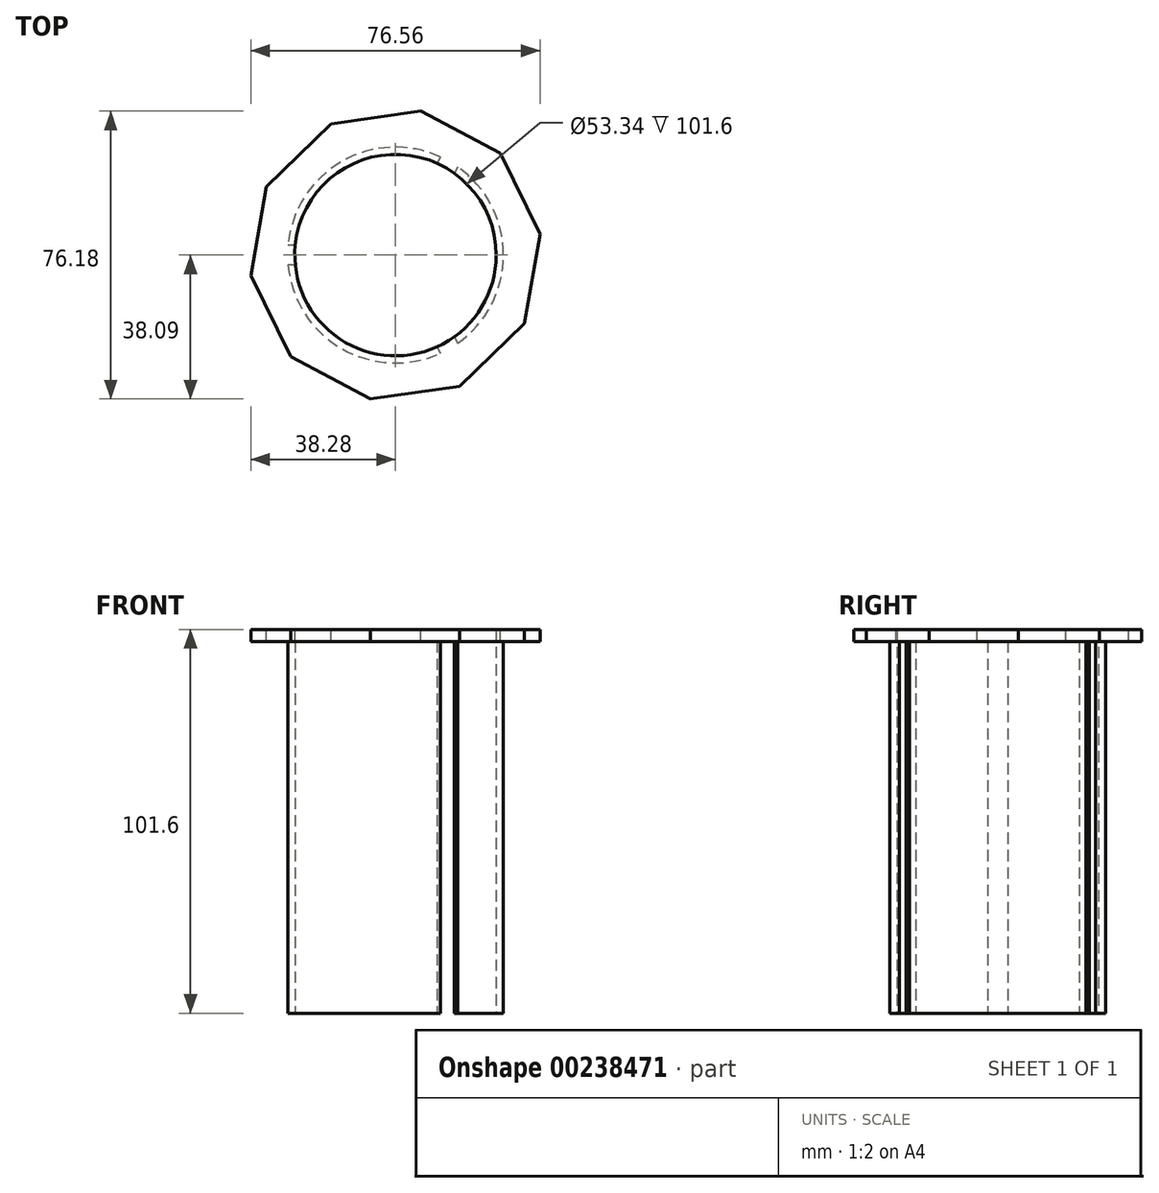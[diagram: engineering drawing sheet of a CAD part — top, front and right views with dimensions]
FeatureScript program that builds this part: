
annotation { "Feature Type Name" : "Feature", "Feature Type Description" : "" }
export const myFeature = defineFeature(function(context is Context, id is Id, definition is map)
    precondition{}
    {
        {
            var Q0;
            Q0=qCreatedBy(makeId("Top.planeOp"),FACE);
            var sketch = newSketch(context, id + "F0", { "sketchPlane" : qUnion([Q0])});
            skCircle(sketch, "E0", {"center": v(0, 0) * mm, "radius": 28.58 * mm});
            skCircle(sketch, "E1", {"center": v(0, 0) * mm, "radius": 26.67 * mm});
            skSolve(sketch);
        }
        {
            var Q0;
            Q0=makeQuery(id+"F0.imprint","IMPRINT",FACE,{"disambiguationData":[TD([[makeQuery(id+"F0.imprint","IMPRINT",EDGE,{"derivedFrom":sQuery(id+"F0.wireOp",EDGE,"E0")}),1.0]])]});
            extrude(context, id + "F1", {"entities" : qUnion([Q0]), "depth" : 101.6 * mm});
        }
        {
            var Q0;
            Q0=makeQuery(id+"F1.opExtrude","CAP_FACE",FACE,{"disambiguationData":[OSD([sQuery(id+"F0.wireOp",EDGE,"E0"),sQuery(id+"F0.wireOp",EDGE,"E1")])],"isStart":false});
            var sketch = newSketch(context, id + "F2", { "sketchPlane" : qUnion([Q0])});
            skCircle(sketch, "E2.cCircle", {"center": v(0, 0) * mm, "radius": 38.67 * mm, "construction": true});
            skLineSegment(sketch, "E2.0", {"start": v(-34.18, 18.1) * mm, "end": v(-17.01, 34.72) * mm});
            skLineSegment(sketch, "E2.1", {"start": v(-17.01, 34.72) * mm, "end": v(6.65, 38.1) * mm});
            skLineSegment(sketch, "E2.2", {"start": v(6.65, 38.1) * mm, "end": v(27.77, 26.91) * mm});
            skLineSegment(sketch, "E2.3", {"start": v(27.77, 26.91) * mm, "end": v(38.28, 5.45) * mm});
            skLineSegment(sketch, "E2.4", {"start": v(38.28, 5.45) * mm, "end": v(34.18, -18.1) * mm});
            skLineSegment(sketch, "E2.5", {"start": v(34.18, -18.1) * mm, "end": v(17.01, -34.72) * mm});
            skLineSegment(sketch, "E2.6", {"start": v(17.01, -34.72) * mm, "end": v(-6.65, -38.1) * mm});
            skLineSegment(sketch, "E2.7", {"start": v(-6.65, -38.1) * mm, "end": v(-27.77, -26.91) * mm});
            skLineSegment(sketch, "E2.8", {"start": v(-27.77, -26.91) * mm, "end": v(-38.28, -5.45) * mm});
            skLineSegment(sketch, "E2.9", {"start": v(-38.28, -5.45) * mm, "end": v(-34.18, 18.1) * mm});
            skCircle(sketch, "E3", {"center": v(0, 0) * mm, "radius": 28.2 * mm});
            skSolve(sketch);
        }
        {
            var Q0;
            Q0=makeQuery(id+"F2.imprint","IMPRINT",FACE,{"disambiguationData":[TD([[makeQuery(id+"F2.imprint","IMPRINT",EDGE,{"derivedFrom":sQuery(id+"F2.wireOp",EDGE,"E2.0")}),-1.0]])]});
            extrude(context, id + "F3", {"entities" : qUnion([Q0]), "operationType" : NewBodyOperationType.ADD, "oppositeDirection" : true, "depth" : 3.17 * mm});
        }
        {
            var Q0;
            Q0=makeQuery(id+"F1.opExtrude","CAP_FACE",FACE,{"disambiguationData":[OSD([sQuery(id+"F0.wireOp",EDGE,"E0"),sQuery(id+"F0.wireOp",EDGE,"E1")])],"isStart":true});
            var sketch = newSketch(context, id + "F4", { "sketchPlane" : qUnion([Q0])});
            skCircle(sketch, "E4.cCircle", {"center": v(0, 0) * mm, "radius": 1.52 * mm, "construction": true});
            skLineSegment(sketch, "E4.0", {"start": v(3.04, 0) * mm, "end": v(-1.52, -2.63) * mm});
            skLineSegment(sketch, "E4.1", {"start": v(-1.52, -2.63) * mm, "end": v(-1.52, 2.63) * mm});
            skLineSegment(sketch, "E4.2", {"start": v(-1.52, 2.63) * mm, "end": v(3.04, 0) * mm});
            skPoint(sketch, "E4.0.midPoint", {"position": v(0.76, -1.31) * mm});
            skLineSegment(sketch, "E5.bottom", {"start": v(-1.52, -2.63) * mm, "end": v(-52.32, -2.63) * mm});
            skLineSegment(sketch, "E5.top", {"start": v(-1.52, 2.63) * mm, "end": v(-52.32, 2.63) * mm});
            skLineSegment(sketch, "E5.right", {"start": v(-52.32, -2.63) * mm, "end": v(-52.32, 2.63) * mm});
            skLineSegment(sketch, "E6.top", {"start": v(23.88, 46.62) * mm, "end": v(28.44, 44) * mm});
            skLineSegment(sketch, "E6.left", {"start": v(-1.52, 2.63) * mm, "end": v(23.88, 46.62) * mm});
            skLineSegment(sketch, "E6.right", {"start": v(3.04, 0) * mm, "end": v(28.44, 44) * mm});
            skLineSegment(sketch, "E7.bottom", {"start": v(23.88, -46.62) * mm, "end": v(28.44, -44) * mm});
            skLineSegment(sketch, "E7.top", {"start": v(-1.52, -2.63) * mm, "end": v(3.04, 0) * mm});
            skLineSegment(sketch, "E7.left", {"start": v(23.88, -46.62) * mm, "end": v(-1.52, -2.63) * mm});
            skLineSegment(sketch, "E7.right", {"start": v(28.44, -44) * mm, "end": v(3.04, 0) * mm});
            skSolve(sketch);
        }
        {
            var Q0;
            {var subQ0=sQuery(id+"F4.wireOp",EDGE,"E7.left");var subQ1=makeQuery(id+"F1.opExtrude","CAP_EDGE",EDGE,{"disambiguationData":[OSD([sQuery(id+"F0.wireOp",EDGE,"E0")])],"isStart":true});var subQ2=makeQuery(id+"F4.imprint","INTERSECT",VERTEX,{"derivedFrom":[subQ1,subQ0]});Q0=makeQuery(id+"F4.imprint","IMPRINT",FACE,{"disambiguationData":[TD([[makeQuery(id+"F4.imprint","IMPRINT",EDGE,{"disambiguationData":[TD([[subQ2,-1.0]])],"derivedFrom":subQ0}),-1.0]])]});}
            var Q1;
            {var subQ0=sQuery(id+"F4.wireOp",EDGE,"E6.left");var subQ1=makeQuery(id+"F1.opExtrude","CAP_EDGE",EDGE,{"disambiguationData":[OSD([sQuery(id+"F0.wireOp",EDGE,"E0")])],"isStart":true});var subQ2=makeQuery(id+"F4.imprint","INTERSECT",VERTEX,{"derivedFrom":[subQ1,subQ0]});Q1=makeQuery(id+"F4.imprint","IMPRINT",FACE,{"disambiguationData":[TD([[makeQuery(id+"F4.imprint","IMPRINT",EDGE,{"disambiguationData":[TD([[subQ2,1.0]])],"derivedFrom":subQ0}),-1.0]])]});}
            var Q2;
            {var subQ0=sQuery(id+"F4.wireOp",EDGE,"E5.bottom");var subQ1=makeQuery(id+"F1.opExtrude","CAP_EDGE",EDGE,{"disambiguationData":[OSD([sQuery(id+"F0.wireOp",EDGE,"E0")])],"isStart":true});var subQ2=makeQuery(id+"F4.imprint","INTERSECT",VERTEX,{"derivedFrom":[subQ1,subQ0]});Q2=makeQuery(id+"F4.imprint","IMPRINT",FACE,{"disambiguationData":[TD([[makeQuery(id+"F4.imprint","IMPRINT",EDGE,{"disambiguationData":[TD([[subQ2,1.0]])],"derivedFrom":subQ0}),-1.0]])]});}
            extrude(context, id + "F5", {"entities" : qUnion([Q0, Q1, Q2]), "operationType" : NewBodyOperationType.REMOVE, "oppositeDirection" : true, "depth" : 98.42 * mm});
        }
    });
